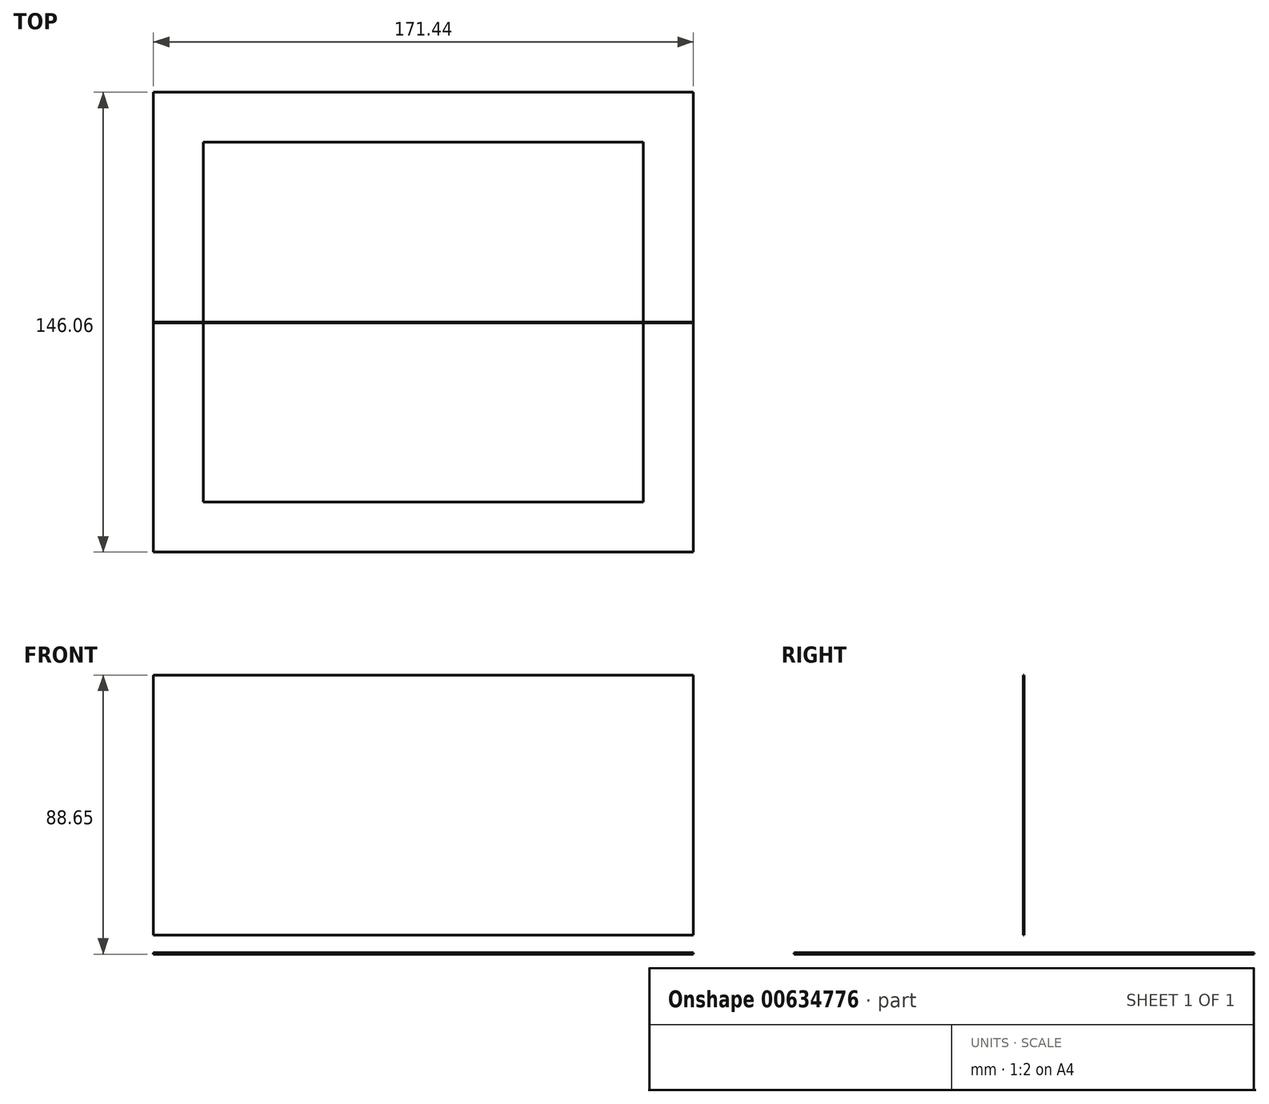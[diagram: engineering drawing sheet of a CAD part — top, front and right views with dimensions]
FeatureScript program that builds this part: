
annotation { "Feature Type Name" : "Feature", "Feature Type Description" : "" }
export const myFeature = defineFeature(function(context is Context, id is Id, definition is map)
    precondition{}
    {
        {
            var Q0;
            Q0=qCreatedBy(makeId("Top.planeOp"),FACE);
            var sketch = newSketch(context, id + "F0", { "sketchPlane" : qUnion([Q0])});
            skLineSegment(sketch, "E0.bottom", {"start": v(-85.72, 73.03) * mm, "end": v(85.73, 73.03) * mm});
            skLineSegment(sketch, "E0.top", {"start": v(-85.73, -73.03) * mm, "end": v(85.72, -73.03) * mm});
            skLineSegment(sketch, "E0.left", {"start": v(-85.72, 73.03) * mm, "end": v(-85.73, -73.03) * mm});
            skLineSegment(sketch, "E0.right", {"start": v(85.73, 73.03) * mm, "end": v(85.72, -73.03) * mm});
            skPoint(sketch, "E0.middle", {"position": v(0, 0) * mm});
            skLineSegment(sketch, "E1.bottom", {"start": v(-69.85, 57.15) * mm, "end": v(69.85, 57.15) * mm});
            skLineSegment(sketch, "E1.top", {"start": v(-69.85, -57.15) * mm, "end": v(69.85, -57.15) * mm});
            skLineSegment(sketch, "E1.left", {"start": v(-69.85, 57.15) * mm, "end": v(-69.85, -57.15) * mm});
            skLineSegment(sketch, "E1.right", {"start": v(69.85, 57.15) * mm, "end": v(69.85, -57.15) * mm});
            skSolve(sketch);
        }
        {
            var Q0;
            Q0=makeQuery(id+"F0.imprint","IMPRINT",FACE,{"disambiguationData":[TD([[makeQuery(id+"F0.imprint","IMPRINT",EDGE,{"derivedFrom":sQuery(id+"F0.wireOp",EDGE,"E0.bottom")}),-1.0]])]});
            extrude(context, id + "F1", {"entities" : qUnion([Q0]), "depth" : 0.5 * mm, "offsetDistance" : 25.4 * mm});
        }
        {
            var Q0;
            Q0=qCreatedBy(makeId("Front.planeOp"),FACE);
            var sketch = newSketch(context, id + "F2", { "sketchPlane" : qUnion([Q0])});
            skLineSegment(sketch, "E2.bottom", {"start": v(85.73, 6.1) * mm, "end": v(-85.73, 6.1) * mm});
            skLineSegment(sketch, "E2.top", {"start": v(85.73, 88.65) * mm, "end": v(-85.73, 88.65) * mm});
            skLineSegment(sketch, "E2.left", {"start": v(85.73, 6.1) * mm, "end": v(85.73, 88.65) * mm});
            skLineSegment(sketch, "E2.right", {"start": v(-85.73, 6.1) * mm, "end": v(-85.73, 88.65) * mm});
            skPoint(sketch, "E2.middle", {"position": v(0, 47.37) * mm});
            skSolve(sketch);
        }
        {
            var Q0;
            Q0=makeQuery(id+"F2.imprint","IMPRINT",FACE,{"disambiguationData":[TD([[makeQuery(id+"F2.imprint","IMPRINT",EDGE,{"derivedFrom":sQuery(id+"F2.wireOp",EDGE,"E2.bottom")}),-1.0]])]});
            extrude(context, id + "F3", {"entities" : qUnion([Q0]), "depth" : 0.25 * mm, "offsetDistance" : 25.4 * mm});
        }
    });
